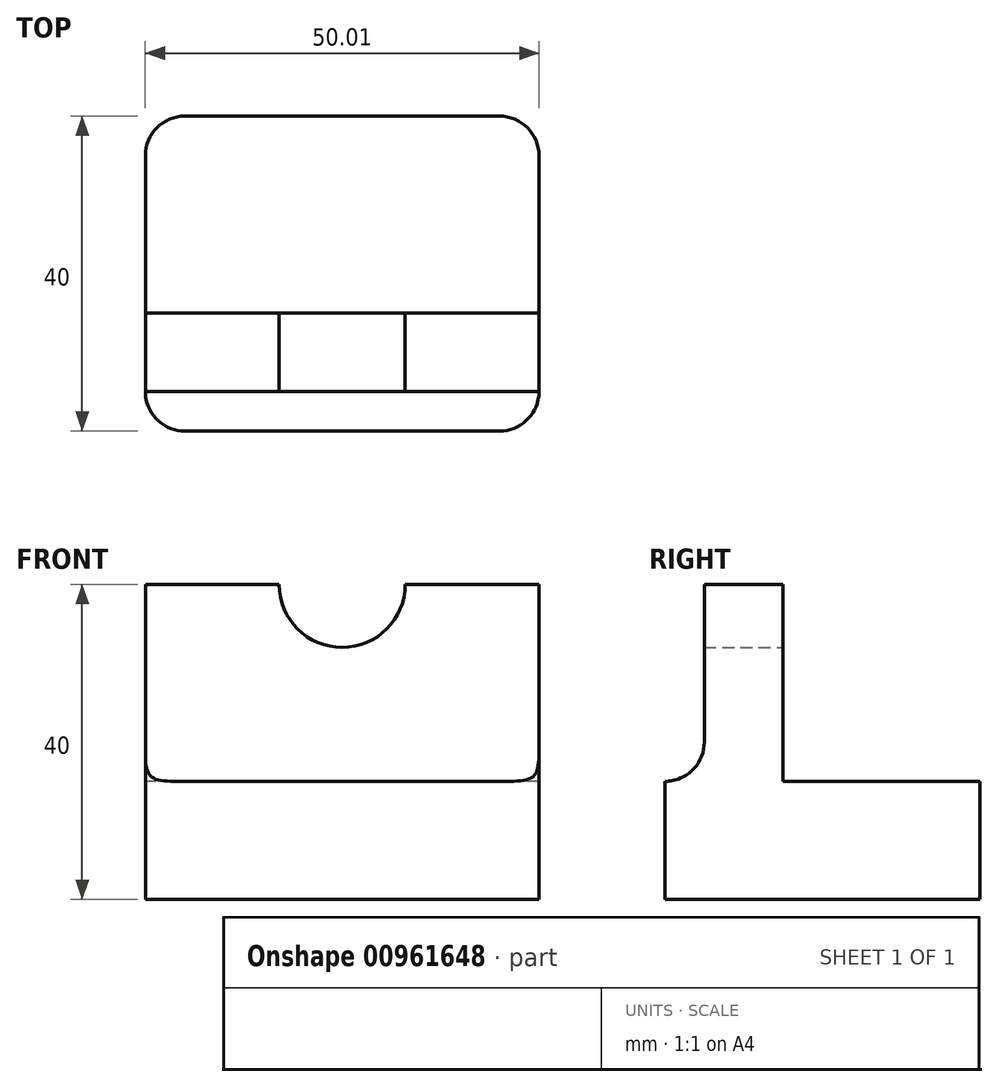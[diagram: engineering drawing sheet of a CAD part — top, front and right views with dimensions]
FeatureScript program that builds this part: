
annotation { "Feature Type Name" : "Feature", "Feature Type Description" : "" }
export const myFeature = defineFeature(function(context is Context, id is Id, definition is map)
    precondition{}
    {
        {
            var Q0;
            Q0=qCreatedBy(makeId("Top.planeOp"),FACE);
            var sketch = newSketch(context, id + "F0", { "sketchPlane" : qUnion([Q0])});
            skLineSegment(sketch, "E0.bottom", {"start": v(4.46, -6.24) * mm, "end": v(54.46, -6.24) * mm});
            skLineSegment(sketch, "E0.top", {"start": v(4.46, -46.24) * mm, "end": v(54.46, -46.24) * mm});
            skLineSegment(sketch, "E0.left", {"start": v(4.46, -6.24) * mm, "end": v(4.46, -46.24) * mm});
            skLineSegment(sketch, "E0.right", {"start": v(54.46, -6.24) * mm, "end": v(54.46, -46.24) * mm});
            skSolve(sketch);
        }
        {
            var Q0;
            Q0=makeQuery(id+"F0.imprint","IMPRINT",FACE,{"disambiguationData":[TD([[makeQuery(id+"F0.imprint","IMPRINT",EDGE,{"derivedFrom":sQuery(id+"F0.wireOp",EDGE,"E0.bottom")}),-1.0]])]});
            extrude(context, id + "F1", {"entities" : qUnion([Q0]), "depth" : 15 * mm, "offsetDistance" : 25 * mm});
        }
        {
            var Q0;
            Q0=makeQuery(id+"F1.opExtrude","CAP_FACE",FACE,{"disambiguationData":[OSD([sQuery(id+"F0.wireOp",EDGE,"E0.bottom"),sQuery(id+"F0.wireOp",EDGE,"E0.top"),sQuery(id+"F0.wireOp",EDGE,"E0.left"),sQuery(id+"F0.wireOp",EDGE,"E0.right")])],"isStart":false});
            var sketch = newSketch(context, id + "F2", { "sketchPlane" : qUnion([Q0])});
            skLineSegment(sketch, "E1", {"start": v(54.46, -6.24) * mm, "end": v(54.46, -31.24) * mm});
            skLineSegment(sketch, "E2", {"start": v(54.46, -31.24) * mm, "end": v(4.46, -31.24) * mm});
            skLineSegment(sketch, "E3", {"start": v(4.46, -31.24) * mm, "end": v(4.46, -41.24) * mm});
            skLineSegment(sketch, "E4", {"start": v(4.46, -41.24) * mm, "end": v(54.46, -41.24) * mm});
            skLineSegment(sketch, "E5", {"start": v(54.46, -41.24) * mm, "end": v(54.46, -31.24) * mm});
            skSolve(sketch);
        }
        {
            var Q0;
            Q0=makeQuery(id+"F2.imprint","IMPRINT",FACE,{"disambiguationData":[TD([[makeQuery(id+"F2.imprint","IMPRINT",EDGE,{"derivedFrom":sQuery(id+"F2.wireOp",EDGE,"E2")}),1.0]])]});
            extrude(context, id + "F3", {"entities" : qUnion([Q0]), "operationType" : NewBodyOperationType.ADD, "depth" : 25 * mm, "offsetDistance" : 25 * mm});
        }
        {
            var Q0;
            Q0=makeQuery(id+"F3.opExtrude","SWEPT_FACE",FACE,{"disambiguationData":[OSD([sQuery(id+"F2.wireOp",EDGE,"E2")])]});
            var sketch = newSketch(context, id + "F4", { "sketchPlane" : qUnion([Q0])});
            skCircle(sketch, "E6", {"center": v(-29.46, 40) * mm, "radius": 8 * mm});
            skSolve(sketch);
        }
        {
            var Q0;
            {var subQ0=sQuery(id+"F4.wireOp",EDGE,"E6");var subQ1=makeQuery(id+"F3.opExtrude","CAP_EDGE",EDGE,{"disambiguationData":[OSD([sQuery(id+"F2.wireOp",EDGE,"E2")])],"isStart":false});var subQ2=makeQuery(id+"F4.imprint","INTERSECT",VERTEX,{"disambiguationData":[OD(0.0)],"derivedFrom":[subQ1,subQ0]});Q0=makeQuery(id+"F4.imprint","IMPRINT",FACE,{"disambiguationData":[TD([[makeQuery(id+"F4.imprint","IMPRINT",EDGE,{"disambiguationData":[TD([[subQ2,-1.0]])],"derivedFrom":subQ0}),1.0]])]});}
            extrude(context, id + "F5", {"entities" : qUnion([Q0]), "operationType" : NewBodyOperationType.REMOVE, "oppositeDirection" : true, "depth" : 25 * mm, "offsetDistance" : 25 * mm});
        }
        {
            var Q0;
            Q0=makeQuery(id+"F3.opExtrude","CAP_EDGE",EDGE,{"disambiguationData":[OSD([sQuery(id+"F2.wireOp",EDGE,"E2")])],"isStart":true});
            var Q1;
            Q1=makeQuery(id+"F1.opExtrude","SWEPT_EDGE",EDGE,{"disambiguationData":[OSD([sQuery(id+"F0.wireOp",EDGE,"E0.bottom"),sQuery(id+"F0.wireOp",EDGE,"E0.right")])]});
            var Q2;
            Q2=makeQuery(id+"F1.opExtrude","SWEPT_EDGE",EDGE,{"disambiguationData":[OSD([sQuery(id+"F0.wireOp",EDGE,"E0.bottom"),sQuery(id+"F0.wireOp",EDGE,"E0.left")])]});
            var Q3;
            Q3=makeQuery(id+"F1.opExtrude","SWEPT_EDGE",EDGE,{"disambiguationData":[OSD([sQuery(id+"F0.wireOp",EDGE,"E0.top"),sQuery(id+"F0.wireOp",EDGE,"E0.right")])]});
            var Q4;
            Q4=makeQuery(id+"F1.opExtrude","SWEPT_EDGE",EDGE,{"disambiguationData":[OSD([sQuery(id+"F0.wireOp",EDGE,"E0.top"),sQuery(id+"F0.wireOp",EDGE,"E0.left")])]});
            fillet(context, id + "F6", {"entities" : qUnion([Q0, Q1, Q2, Q3, Q4]), "radius" : 5 * mm, "tangentPropagation" : true, "allowEdgeOverflow" : false});
        }
        {
            var Q0;
            Q0=makeQuery(id+"F3.opExtrude","CAP_EDGE",EDGE,{"disambiguationData":[OSD([sQuery(id+"F2.wireOp",EDGE,"E4")])],"isStart":true});
            fillet(context, id + "F7", {"entities" : qUnion([Q0]), "radius" : 5 * mm, "tangentPropagation" : true, "allowEdgeOverflow" : false});
        }
    });
